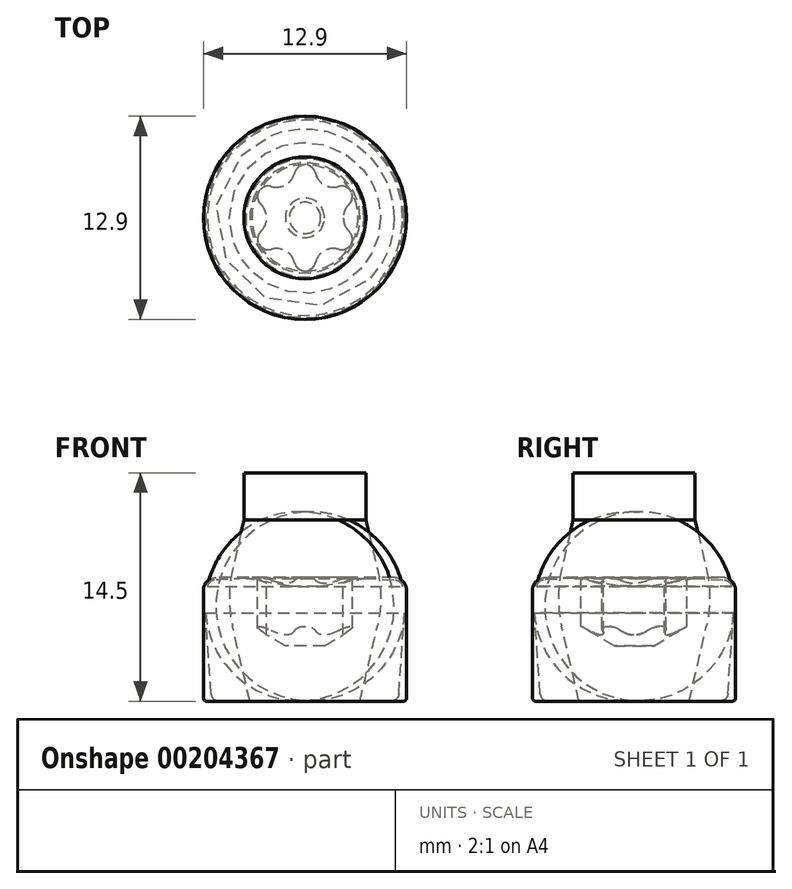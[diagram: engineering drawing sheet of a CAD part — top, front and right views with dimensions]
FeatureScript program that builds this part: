
annotation { "Feature Type Name" : "Feature", "Feature Type Description" : "" }
export const myFeature = defineFeature(function(context is Context, id is Id, definition is map)
    precondition{}
    {
        {
            var Q0;
            Q0=qCreatedBy(makeId("Front.planeOp"),FACE);
            var sketch = newSketch(context, id + "F0", { "sketchPlane" : qUnion([Q0])});
            skLineSegment(sketch, "E0", {"start": v(0, 0) * mm, "end": v(0, 3.52) * mm, "construction": true});
            skLineSegment(sketch, "E1", {"start": v(3.37, 7.85) * mm, "end": v(5.65, 7.85) * mm});
            skLineSegment(sketch, "E2", {"start": v(6.45, 7.05) * mm, "end": v(6.45, 0.2) * mm});
            skLineSegment(sketch, "E3", {"start": v(6.25, 0) * mm, "end": v(0, 0) * mm});
            skPoint(sketch, "E4.visualSharp", {"position": v(6.45, 7.85) * mm});
            skArc(sketch, "E4.filletArc", {"start": v(6.45, 7.05) * mm, "mid": v(6.22, 7.62) * mm, "end": v(5.65, 7.85) * mm});
            skPoint(sketch, "E5.visualSharp", {"position": v(6.45, 0) * mm});
            skArc(sketch, "E5.filletArc", {"start": v(6.25, 0) * mm, "mid": v(6.4, 0.06) * mm, "end": v(6.45, 0.2) * mm});
            skLineSegment(sketch, "E6", {"start": v(3.37, 7.85) * mm, "end": v(3.38, 4.75) * mm});
            skLineSegment(sketch, "E7", {"start": v(3.38, 4.75) * mm, "end": v(1.25, 3.52) * mm});
            skLineSegment(sketch, "E8", {"start": v(1.25, 3.52) * mm, "end": v(0, 3.52) * mm});
            skLineSegment(sketch, "E9", {"start": v(0, 3.52) * mm, "end": v(0, 0) * mm});
            skSolve(sketch);
        }
        {
            var Q0;
            Q0=qSketchRegion(id+"F0",true);
            var Q1;
            Q1=sQuery(id+"F0.wireOp",EDGE,"E9");
            revolve(context, id + "F1", {"entities" : qUnion([Q0]), "axis" : qUnion([Q1]), "revolveType" : RevolveType.FULL});
        }
        {
            var Q0;
            Q0=makeQuery(id+"F1.opRevolve","SWEPT_FACE",FACE,{"disambiguationData":[OSD([sQuery(id+"F0.wireOp",EDGE,"E1")])]});
            var sketch = newSketch(context, id + "F2", { "sketchPlane" : qUnion([Q0])});
            skArc(sketch, "E10", {"start": v(0.65, 2.87) * mm, "mid": v(0, 3.37) * mm, "end": v(-0.65, 2.87) * mm});
            skLineSegment(sketch, "E11", {"start": v(-0.65, 2.87) * mm, "end": v(-0.67, 2.82) * mm});
            skLineSegment(sketch, "E12", {"start": v(0.65, 2.87) * mm, "end": v(0.67, 2.82) * mm});
            skLineSegment(sketch, "E13.1.0", {"start": v(-2.16, 2) * mm, "end": v(-2.11, 1.99) * mm});
            skArc(sketch, "E13.1.1", {"start": v(-2.16, 2) * mm, "mid": v(-2.92, 1.69) * mm, "end": v(-2.82, 0.87) * mm});
            skLineSegment(sketch, "E13.1.2", {"start": v(-2.82, 0.87) * mm, "end": v(-2.78, 0.84) * mm});
            skLineSegment(sketch, "E13.2.0", {"start": v(-2.82, -0.87) * mm, "end": v(-2.78, -0.84) * mm});
            skArc(sketch, "E13.2.1", {"start": v(-2.82, -0.87) * mm, "mid": v(-2.92, -1.69) * mm, "end": v(-2.16, -2) * mm});
            skLineSegment(sketch, "E13.2.2", {"start": v(-2.16, -2) * mm, "end": v(-2.11, -1.99) * mm});
            skLineSegment(sketch, "E13.3.0", {"start": v(-0.65, -2.87) * mm, "end": v(-0.67, -2.82) * mm});
            skArc(sketch, "E13.3.1", {"start": v(-0.65, -2.87) * mm, "mid": v(0, -3.37) * mm, "end": v(0.65, -2.87) * mm});
            skLineSegment(sketch, "E13.3.2", {"start": v(0.65, -2.87) * mm, "end": v(0.67, -2.82) * mm});
            skLineSegment(sketch, "E13.4.0", {"start": v(2.16, -2) * mm, "end": v(2.11, -1.99) * mm});
            skArc(sketch, "E13.4.1", {"start": v(2.16, -2) * mm, "mid": v(2.92, -1.69) * mm, "end": v(2.82, -0.87) * mm});
            skLineSegment(sketch, "E13.4.2", {"start": v(2.82, -0.87) * mm, "end": v(2.78, -0.84) * mm});
            skLineSegment(sketch, "E13.5.0", {"start": v(2.82, 0.87) * mm, "end": v(2.78, 0.84) * mm});
            skArc(sketch, "E13.5.1", {"start": v(2.82, 0.87) * mm, "mid": v(2.92, 1.69) * mm, "end": v(2.16, 2) * mm});
            skLineSegment(sketch, "E13.5.2", {"start": v(2.16, 2) * mm, "end": v(2.11, 1.99) * mm});
            skPoint(sketch, "E13.center", {"position": v(0, 0) * mm});
            skPoint(sketch, "E14.newPointA", {"position": v(0.6, 1.26) * mm});
            skPoint(sketch, "E14.newPointB", {"position": v(-1.4, 0.1) * mm});
            skArc(sketch, "E14.filletArc", {"start": v(-2.11, 1.99) * mm, "mid": v(-1.22, 2.1) * mm, "end": v(-0.67, 2.82) * mm});
            skPoint(sketch, "E15.newPointA", {"position": v(-0.6, 1.26) * mm});
            skPoint(sketch, "E15.newPointB", {"position": v(1.4, 0.12) * mm});
            skArc(sketch, "E15.filletArc", {"start": v(0.67, 2.82) * mm, "mid": v(1.22, 2.1) * mm, "end": v(2.11, 1.99) * mm});
            skPoint(sketch, "E16.newPointA", {"position": v(0.8, -1.15) * mm});
            skPoint(sketch, "E16.newPointB", {"position": v(0.8, 1.15) * mm});
            skArc(sketch, "E16.filletArc", {"start": v(2.78, 0.84) * mm, "mid": v(2.43, 0) * mm, "end": v(2.78, -0.84) * mm});
            skPoint(sketch, "E17.newPointA", {"position": v(-0.6, -1.26) * mm});
            skPoint(sketch, "E17.newPointB", {"position": v(1.4, -0.1) * mm});
            skArc(sketch, "E17.filletArc", {"start": v(2.11, -1.99) * mm, "mid": v(1.22, -2.1) * mm, "end": v(0.67, -2.82) * mm});
            skPoint(sketch, "E18.newPointA", {"position": v(-1.4, -0.12) * mm});
            skPoint(sketch, "E18.newPointB", {"position": v(0.6, -1.26) * mm});
            skArc(sketch, "E18.filletArc", {"start": v(-0.67, -2.82) * mm, "mid": v(-1.22, -2.1) * mm, "end": v(-2.11, -1.99) * mm});
            skPoint(sketch, "E19.newPointA", {"position": v(-0.8, 1.15) * mm});
            skPoint(sketch, "E19.newPointB", {"position": v(-0.8, -1.15) * mm});
            skArc(sketch, "E19.filletArc", {"start": v(-2.78, -0.84) * mm, "mid": v(-2.43, 0) * mm, "end": v(-2.78, 0.84) * mm});
            skCircle(sketch, "E20", {"center": v(0, 0) * mm, "radius": 3.61 * mm});
            skSolve(sketch);
        }
        {
            var Q0;
            Q0=qSketchRegion(id+"F2",true);
            var Q1;
            Q1=makeQuery(id+"F1.opRevolve","SWEPT_FACE",FACE,{"disambiguationData":[OSD([sQuery(id+"F0.wireOp",EDGE,"E7")])]});
            extrude(context, id + "F3", {"entities" : qUnion([Q0]), "operationType" : NewBodyOperationType.ADD, "endBound" : BoundingType.UP_TO_SURFACE, "oppositeDirection" : true, "endBoundEntityFace" : qUnion([Q1]), "depth" : 25 * mm});
        }
        {
            var Q0;
            Q0=makeQuery(id+"F3.boolean.opBoolean","MERGE",FACE,{"derivedFrom":[makeQuery(id+"F1.opRevolve","SWEPT_FACE",FACE,{"disambiguationData":[OSD([sQuery(id+"F0.wireOp",EDGE,"E1")])]}),makeQuery(id+"F3.opExtrude","CAP_FACE",FACE,{"disambiguationData":[OSD([sQuery(id+"F2.wireOp",EDGE,"E10"),sQuery(id+"F2.wireOp",EDGE,"E11"),sQuery(id+"F2.wireOp",EDGE,"E12"),sQuery(id+"F2.wireOp",EDGE,"E13.1.0"),sQuery(id+"F2.wireOp",EDGE,"E13.1.1"),sQuery(id+"F2.wireOp",EDGE,"E13.1.2"),sQuery(id+"F2.wireOp",EDGE,"E13.2.0"),sQuery(id+"F2.wireOp",EDGE,"E13.2.1"),sQuery(id+"F2.wireOp",EDGE,"E13.2.2"),sQuery(id+"F2.wireOp",EDGE,"E13.3.0"),sQuery(id+"F2.wireOp",EDGE,"E13.3.1"),sQuery(id+"F2.wireOp",EDGE,"E13.3.2"),sQuery(id+"F2.wireOp",EDGE,"E13.4.0"),sQuery(id+"F2.wireOp",EDGE,"E13.4.1"),sQuery(id+"F2.wireOp",EDGE,"E13.4.2"),sQuery(id+"F2.wireOp",EDGE,"E13.5.0"),sQuery(id+"F2.wireOp",EDGE,"E13.5.1"),sQuery(id+"F2.wireOp",EDGE,"E13.5.2"),sQuery(id+"F2.wireOp",EDGE,"E14.filletArc"),sQuery(id+"F2.wireOp",EDGE,"E15.filletArc"),sQuery(id+"F2.wireOp",EDGE,"E16.filletArc"),sQuery(id+"F2.wireOp",EDGE,"E17.filletArc"),sQuery(id+"F2.wireOp",EDGE,"E18.filletArc"),sQuery(id+"F2.wireOp",EDGE,"E19.filletArc"),sQuery(id+"F2.wireOp",EDGE,"E20")])],"isStart":true})]});
            var sketch = newSketch(context, id + "F4", { "sketchPlane" : qUnion([Q0])});
            skCircle(sketch, "E21", {"center": v(0, 0) * mm, "radius": 3.37 * mm});
            skSolve(sketch);
        }
        {
            var Q0;
            Q0=qSketchRegion(id+"F4",true);
            extrude(context, id + "F5", {"entities" : qUnion([Q0]), "operationType" : NewBodyOperationType.REMOVE, "oppositeDirection" : true, "depth" : 1 * mm, "hasDraft" : true, "draftAngle" : 70 * degree, "draftPullDirection" : true});
        }
        {
            var Q0;
            Q0=qCreatedBy(makeId("Front.planeOp"),FACE);
            var sketch = newSketch(context, id + "F6", { "sketchPlane" : qUnion([Q0])});
            skLineSegment(sketch, "E22", {"start": v(0, 0) * mm, "end": v(0, 14.5) * mm, "construction": true});
            skLineSegment(sketch, "E23", {"start": v(0, 14.5) * mm, "end": v(3.87, 14.5) * mm});
            skLineSegment(sketch, "E24", {"start": v(3.87, 14.5) * mm, "end": v(3.87, 11.5) * mm});
            skLineSegment(sketch, "E25", {"start": v(3.87, 11.5) * mm, "end": v(4.6, 8.37) * mm});
            skLineSegment(sketch, "E26", {"start": v(3.5, 0) * mm, "end": v(0, 0) * mm});
            skLineSegment(sketch, "E27", {"start": v(0, 14.5) * mm, "end": v(0, 0) * mm});
            skLineSegment(sketch, "E28", {"start": v(3.5, 0) * mm, "end": v(4.6, 4.77) * mm});
            skArc(sketch, "E29.filletArc", {"start": v(4.6, 4.77) * mm, "mid": v(4.8, 6.57) * mm, "end": v(4.6, 8.37) * mm});
            skSolve(sketch);
        }
        {
            var Q0;
            Q0=qSketchRegion(id+"F6",true);
            var Q1;
            Q1=sQuery(id+"F6.wireOp",EDGE,"E27");
            revolve(context, id + "F7", {"entities" : qUnion([Q0]), "axis" : qUnion([Q1]), "revolveType" : RevolveType.FULL});
        }
        {
            var Q0;
            Q0=qCreatedBy(makeId("Front.planeOp"),FACE);
            var sketch = newSketch(context, id + "F8", { "sketchPlane" : qUnion([Q0])});
            skLineSegment(sketch, "E30", {"start": v(0, 0) * mm, "end": v(0, 7.32) * mm});
            skLineSegment(sketch, "E31", {"start": v(6.32, 5.6) * mm, "end": v(5.96, 0.47) * mm});
            skLineSegment(sketch, "E32", {"start": v(5.46, 0) * mm, "end": v(0, 0) * mm});
            skPoint(sketch, "E33.visualSharp", {"position": v(5.93, 0) * mm});
            skArc(sketch, "E33.filletArc", {"start": v(5.46, 0) * mm, "mid": v(5.8, 0.13) * mm, "end": v(5.96, 0.47) * mm});
            skLineSegment(sketch, "E34", {"start": v(0, 7.32) * mm, "end": v(0, 0) * mm, "construction": true});
            skLineSegment(sketch, "E35", {"start": v(0, 7.32) * mm, "end": v(1, 7.32) * mm});
            skLineSegment(sketch, "E36", {"start": v(1, 7.32) * mm, "end": v(3.75, 7.8) * mm});
            skLineSegment(sketch, "E37", {"start": v(3.75, 7.8) * mm, "end": v(5.74, 7.7) * mm});
            skArc(sketch, "E38.filletArc", {"start": v(6.32, 5.6) * mm, "mid": v(6.32, 6.46) * mm, "end": v(6.2, 7.3) * mm});
            skPoint(sketch, "E39.visualSharp", {"position": v(6.1, 7.68) * mm});
            skArc(sketch, "E39.filletArc", {"start": v(6.2, 7.3) * mm, "mid": v(6.04, 7.58) * mm, "end": v(5.74, 7.7) * mm});
            skLineSegment(sketch, "E40", {"start": v(6.32, 5.6) * mm, "end": v(6.35, 6) * mm, "construction": true});
            skSolve(sketch);
        }
        {
            var Q0;
            Q0=qSketchRegion(id+"F8",true);
            var Q1;
            Q1=sQuery(id+"F8.wireOp",EDGE,"E30");
            revolve(context, id + "F9", {"entities" : qUnion([Q0]), "axis" : qUnion([Q1]), "revolveType" : RevolveType.FULL});
        }
    });
